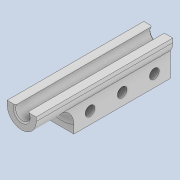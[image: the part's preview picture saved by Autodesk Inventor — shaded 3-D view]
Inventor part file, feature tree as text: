
AUTODESK INVENTOR PART (.ipt)
format: ipt  version: 2020 (Build 240168000, 168)  size: 190,976 bytes
history: native  units: mm
features: other x6, extrude x5, sketch x5, projected_geometry x4, reference x2, fillet x1, chamfer x1, thicken_offset x1
ambient origin geometry x8: Origin, YZ Plane, XZ Plane, XY Plane, X Axis, Y Axis, Z Axis, Center Point
bodies: Solid1 (feature_tree)
feature tree (25):
  extrude  "Extrusion1"  Depth=1.0mm
  extrude  "Extrusion2"  Depth=1.8mm
  extrude  "Extrusion3"  Depth=1.8mm
  extrude  "Extrusion4"  Depth=12.0mm TaperAngle=0.0deg
  extrude  "Extrusion5"  Depth=3.0mm
  fillet  "Fillet1"  Radius=7.0mm
  chamfer  "Chamfer1"  Distance=12.0mm
  thicken_offset  "Thicken1"
  sketch  "Sketch1"  dims[d0=1.6mm d1=1.0mm]
  reference  "Reference1"
  sketch  "Sketch2"  dims[d2=0.5mm d3=1.8mm]
  projected_geometry  "Projected Loop1"
  sketch  "Sketch3"  dims[d4=0.5mm d5=1.8mm]
  reference  "Reference2"
  projected_geometry  "Projected Loop2"
  sketch  "Sketch4"  dims[d6=0.5mm d7=12.0mm d8=0.0mm]
  projected_geometry  "Projected Loop3"
  sketch  "Sketch5"  dims[d9=7.0mm d10=3.0mm d11=7.0mm d12=12.0mm d13=0.0mm d14=3.0mm d15=1.5mm d16=1.2mm d17=4.0mm d18=1.2mm d19=4.0mm d20=1.2mm d21=12.0mm d22=0.0mm d23=3.0mm d24=12.0mm d25=0.0mm d26=3.6mm d27=5.0mm d28=0.0mm d29=1.5mm d30=0.25mm d31=2.0mm d32=45.0deg d33=0.1mm d34=0.1mm]
  projected_geometry  "Projected Loop4"
  parser-record x2  (decoder bookkeeping rows leaked as tree rows — omitted from the tree; the rows remain in map.json)
  other  "bw_ass_1.iam"
  other  "bw_tube_0.8_1.6:1"
  other  "tip_3_ass.iam"
  other  "ext_shell_1:1"
note: 2 file-system paths scrubbed to <path> (originals preserved in map.json)
